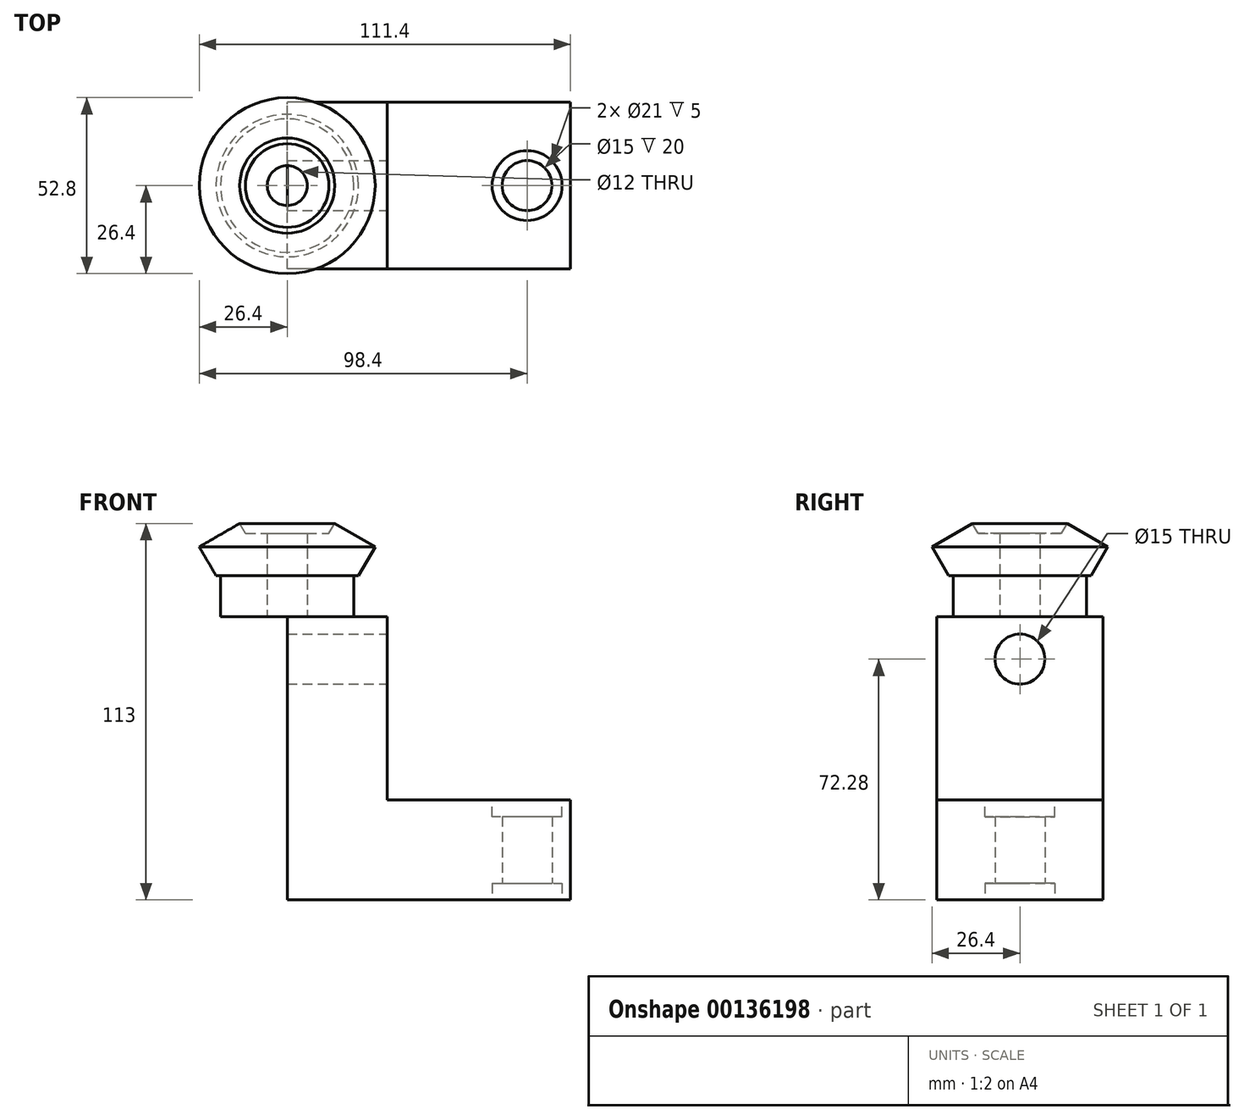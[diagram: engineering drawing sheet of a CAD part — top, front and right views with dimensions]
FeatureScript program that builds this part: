
annotation { "Feature Type Name" : "Feature", "Feature Type Description" : "" }
export const myFeature = defineFeature(function(context is Context, id is Id, definition is map)
    precondition{}
    {
        {
            var Q0;
            Q0=qCreatedBy(makeId("Front.planeOp"),FACE);
            var sketch = newSketch(context, id + "F0", { "sketchPlane" : qUnion([Q0])});
            skLineSegment(sketch, "E0", {"start": v(-6, 0) * mm, "end": v(-20, 0) * mm});
            skLineSegment(sketch, "E1", {"start": v(-20, 0) * mm, "end": v(-20, 12.3) * mm});
            skLineSegment(sketch, "E2", {"start": v(-20, 12.3) * mm, "end": v(-21.38, 12.3) * mm});
            skLineSegment(sketch, "E3", {"start": v(-21.38, 12.3) * mm, "end": v(-26.4, 21) * mm});
            skLineSegment(sketch, "E4", {"start": v(-26.4, 21) * mm, "end": v(-14.28, 28) * mm});
            skLineSegment(sketch, "E5", {"start": v(-14.28, 28) * mm, "end": v(-12.54, 25) * mm});
            skLineSegment(sketch, "E6", {"start": v(-12.54, 25) * mm, "end": v(-6, 25) * mm});
            skLineSegment(sketch, "E7", {"start": v(-6, 25) * mm, "end": v(-6, 0) * mm});
            skLineSegment(sketch, "E8", {"start": v(0, 0) * mm, "end": v(0, 26.64) * mm, "construction": true});
            skSolve(sketch);
        }
        {
            var Q0;
            Q0=makeQuery(id+"F0.imprint","IMPRINT",FACE,{"disambiguationData":[TD([[makeQuery(id+"F0.imprint","IMPRINT",EDGE,{"derivedFrom":sQuery(id+"F0.wireOp",EDGE,"E0")}),-1.0]])]});
            var Q1;
            Q1=sQuery(id+"F0.wireOp",EDGE,"E8");
            revolve(context, id + "F1", {"entities" : qUnion([Q0]), "axis" : qUnion([Q1]), "revolveType" : RevolveType.FULL});
        }
        {
            var Q0;
            Q0=qCreatedBy(makeId("Right.planeOp"),FACE);
            var sketch = newSketch(context, id + "F2", { "sketchPlane" : qUnion([Q0])});
            skLineSegment(sketch, "E9.bottom", {"start": v(-25, 0) * mm, "end": v(25, 0) * mm});
            skLineSegment(sketch, "E9.top", {"start": v(-25, -85) * mm, "end": v(25, -85) * mm});
            skLineSegment(sketch, "E9.left", {"start": v(-25, 0) * mm, "end": v(-25, -85) * mm});
            skLineSegment(sketch, "E9.right", {"start": v(25, 0) * mm, "end": v(25, -85) * mm});
            skSolve(sketch);
        }
        {
            var Q0;
            Q0 = qSketchRegion(id + "F2", true);
            extrude(context, id + "F3", {"entities" : qUnion([Q0]), "depth" : 85 * mm});
        }
        {
            var Q0;
            Q0=makeQuery(id+"F3.opExtrude","CAP_FACE",FACE,{"disambiguationData":[OSD([sQuery(id+"F2.wireOp",EDGE,"E9.bottom"),sQuery(id+"F2.wireOp",EDGE,"E9.top"),sQuery(id+"F2.wireOp",EDGE,"E9.left"),sQuery(id+"F2.wireOp",EDGE,"E9.right")])],"isStart":false});
            var sketch = newSketch(context, id + "F4", { "sketchPlane" : qUnion([Q0])});
            skLineSegment(sketch, "E10.bottom", {"start": v(25, 0) * mm, "end": v(-25, 0) * mm});
            skLineSegment(sketch, "E10.top", {"start": v(25, -55) * mm, "end": v(-25, -55) * mm});
            skLineSegment(sketch, "E10.left", {"start": v(25, 0) * mm, "end": v(25, -55) * mm});
            skLineSegment(sketch, "E10.right", {"start": v(-25, 0) * mm, "end": v(-25, -55) * mm});
            skSolve(sketch);
        }
        {
            var Q0;
            Q0=makeQuery(id+"F4.imprint","IMPRINT",FACE,{"disambiguationData":[TD([[makeQuery(id+"F4.imprint","IMPRINT",EDGE,{"derivedFrom":sQuery(id+"F4.wireOp",EDGE,"E10.bottom")}),-1.0]])]});
            extrude(context, id + "F5", {"entities" : qUnion([Q0]), "operationType" : NewBodyOperationType.REMOVE, "oppositeDirection" : true, "depth" : 55 * mm});
        }
        {
            var Q0;
            Q0=makeQuery(id+"F3.opExtrude","SWEPT_FACE",FACE,{"disambiguationData":[OSD([sQuery(id+"F2.wireOp",EDGE,"E9.top")])]});
            var sketch = newSketch(context, id + "F6", { "sketchPlane" : qUnion([Q0])});
            skCircle(sketch, "E11", {"center": v(72, 0) * mm, "radius": 10.5 * mm});
            skPoint(sketch, "E11.centerSnap0", {"position": v(85, 0) * mm});
            skSolve(sketch);
        }
        {
            var Q0;
            Q0=makeQuery(id+"F6.imprint","IMPRINT",FACE,{"disambiguationData":[TD([[makeQuery(id+"F6.imprint","IMPRINT",EDGE,{"derivedFrom":sQuery(id+"F6.wireOp",EDGE,"E11")}),1.0]])]});
            extrude(context, id + "F7", {"entities" : qUnion([Q0]), "operationType" : NewBodyOperationType.REMOVE, "oppositeDirection" : true, "depth" : 5 * mm});
        }
        {
            var Q0;
            Q0=makeQuery(id+"F7.boolean.opBoolean","COPY",FACE,{"derivedFrom":makeQuery(id+"F7.opExtrude","CAP_FACE",FACE,{"disambiguationData":[OSD([sQuery(id+"F6.wireOp",EDGE,"E11")])],"isStart":false})});
            var sketch = newSketch(context, id + "F8", { "sketchPlane" : qUnion([Q0])});
            skCircle(sketch, "E12", {"center": v(72, 0) * mm, "radius": 7.5 * mm});
            skSolve(sketch);
        }
        {
            var Q0;
            Q0=makeQuery(id+"F8.imprint","IMPRINT",FACE,{"disambiguationData":[TD([[makeQuery(id+"F8.imprint","IMPRINT",EDGE,{"derivedFrom":sQuery(id+"F8.wireOp",EDGE,"E12")}),1.0]])]});
            extrude(context, id + "F9", {"entities" : qUnion([Q0]), "operationType" : NewBodyOperationType.REMOVE, "oppositeDirection" : true, "depth" : 40 * mm});
        }
        {
            var Q0;
            Q0=makeQuery(id+"F5.boolean.opBoolean","COPY",FACE,{"derivedFrom":makeQuery(id+"F5.opExtrude","SWEPT_FACE",FACE,{"disambiguationData":[OSD([sQuery(id+"F4.wireOp",EDGE,"E10.top")])]})});
            var sketch = newSketch(context, id + "F10", { "sketchPlane" : qUnion([Q0])});
            skCircle(sketch, "E13", {"center": v(72, 0) * mm, "radius": 10.5 * mm});
            skSolve(sketch);
        }
        {
            var Q0;
            Q0=makeQuery(id+"F10.imprint","IMPRINT",FACE,{"disambiguationData":[TD([[makeQuery(id+"F10.imprint","IMPRINT",EDGE,{"derivedFrom":sQuery(id+"F10.wireOp",EDGE,"E13")}),1.0]])]});
            extrude(context, id + "F11", {"entities" : qUnion([Q0]), "operationType" : NewBodyOperationType.REMOVE, "oppositeDirection" : true, "depth" : 5 * mm});
        }
        {
            var Q0;
            Q0=makeQuery(id+"F5.boolean.opBoolean","COPY",FACE,{"derivedFrom":makeQuery(id+"F5.opExtrude","CAP_FACE",FACE,{"disambiguationData":[OSD([sQuery(id+"F4.wireOp",EDGE,"E10.bottom"),sQuery(id+"F4.wireOp",EDGE,"E10.top"),sQuery(id+"F4.wireOp",EDGE,"E10.left"),sQuery(id+"F4.wireOp",EDGE,"E10.right")])],"isStart":false})});
            var sketch = newSketch(context, id + "F12", { "sketchPlane" : qUnion([Q0])});
            skCircle(sketch, "E14", {"center": v(0, -12.72) * mm, "radius": 7.5 * mm});
            skSolve(sketch);
        }
        {
            var Q0;
            Q0=makeQuery(id+"F12.imprint","IMPRINT",FACE,{"disambiguationData":[TD([[makeQuery(id+"F12.imprint","IMPRINT",EDGE,{"derivedFrom":sQuery(id+"F12.wireOp",EDGE,"E14")}),1.0]])]});
            extrude(context, id + "F13", {"entities" : qUnion([Q0]), "operationType" : NewBodyOperationType.REMOVE, "endBound" : BoundingType.THROUGH_ALL, "oppositeDirection" : true, "depth" : 25 * mm});
        }
    });
